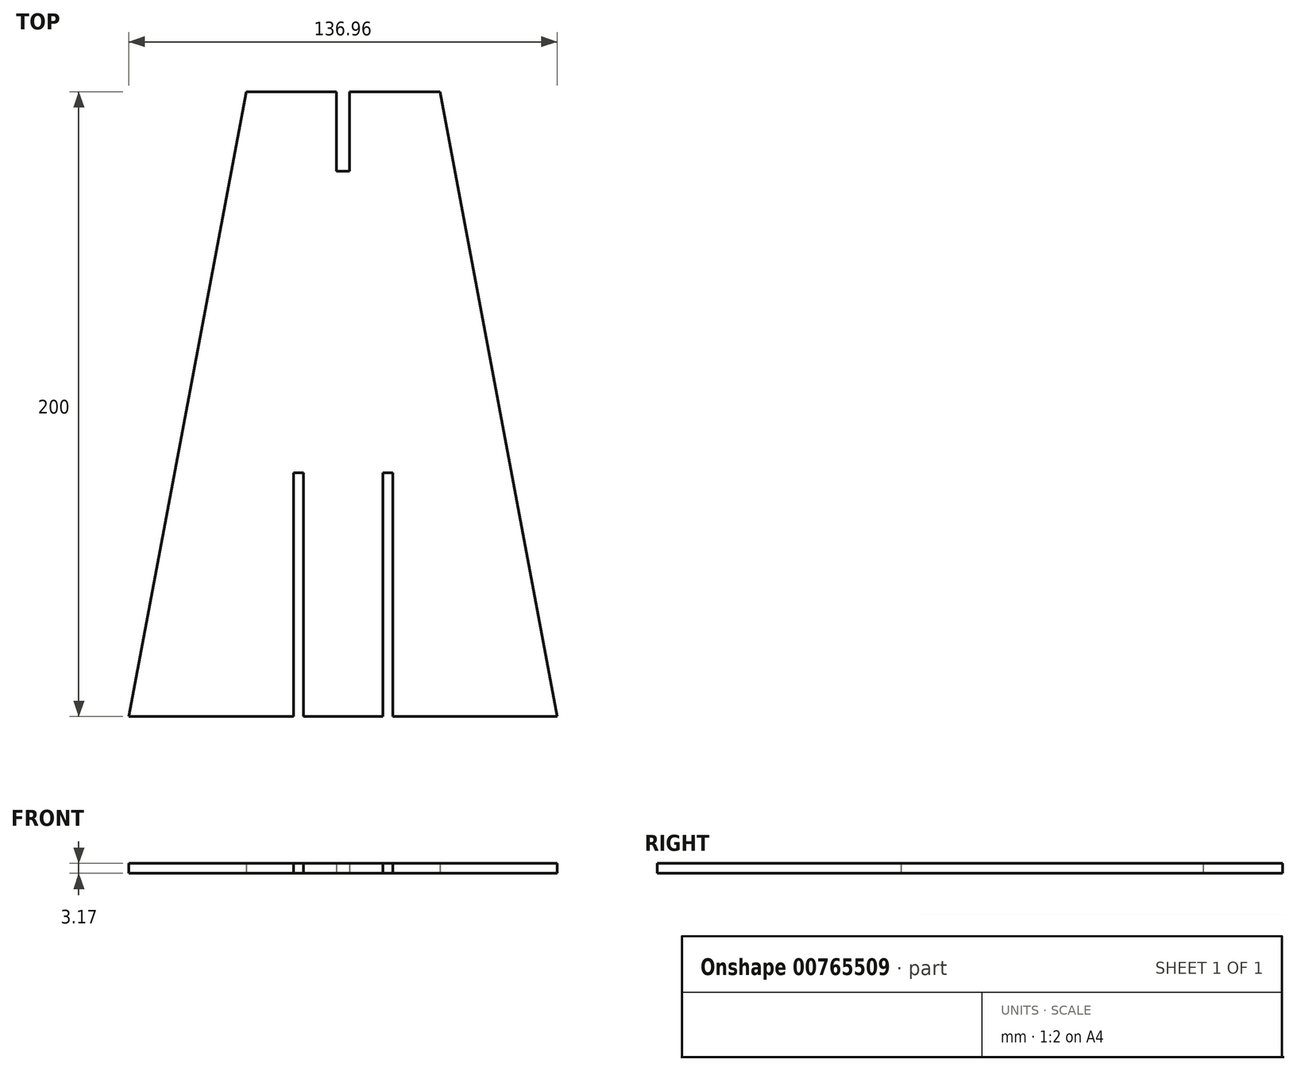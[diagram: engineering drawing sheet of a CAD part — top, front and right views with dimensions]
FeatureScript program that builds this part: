
annotation { "Feature Type Name" : "Feature", "Feature Type Description" : "" }
export const myFeature = defineFeature(function(context is Context, id is Id, definition is map)
    precondition{}
    {
        {
            var Q0;
            Q0=qCreatedBy(makeId("Top.planeOp"),FACE);
            var sketch = newSketch(context, id + "F0", { "sketchPlane" : qUnion([Q0])});
            skLineSegment(sketch, "E0", {"start": v(0, 0) * mm, "end": v(73.41, 0) * mm});
            skLineSegment(sketch, "E1", {"start": v(37.5, 200) * mm, "end": v(66.37, 200) * mm});
            skPoint(sketch, "E2", {"position": v(68.48, 200) * mm});
            skPoint(sketch, "E3", {"position": v(68.48, 0) * mm});
            skLineSegment(sketch, "E4", {"start": v(99.46, 200) * mm, "end": v(136.96, 0) * mm});
            skLineSegment(sketch, "E5", {"start": v(37.5, 200) * mm, "end": v(0, 0) * mm});
            skPoint(sketch, "E6", {"position": v(73.41, 0) * mm});
            skPoint(sketch, "E7", {"position": v(76.59, 0) * mm});
            skLineSegment(sketch, "E8.bottom", {"start": v(76.59, 276) * mm, "end": v(73.41, 276) * mm});
            skLineSegment(sketch, "E9.trimOffspring", {"start": v(76.59, 0) * mm, "end": v(136.96, 0) * mm});
            skLineSegment(sketch, "E10.trimOffspring", {"start": v(76.59, 200) * mm, "end": v(99.46, 200) * mm});
            skLineSegment(sketch, "E11", {"start": v(73.41, 0) * mm, "end": v(76.59, 0) * mm});
            skPoint(sketch, "E12", {"position": v(55.78, 0) * mm});
            skPoint(sketch, "E13", {"position": v(81.18, 0) * mm});
            skLineSegment(sketch, "E14.bottom", {"start": v(55.78, 0) * mm, "end": v(52.6, 0) * mm});
            skLineSegment(sketch, "E14.top", {"start": v(55.78, 78) * mm, "end": v(52.6, 78) * mm});
            skLineSegment(sketch, "E14.left", {"start": v(55.78, 0) * mm, "end": v(55.78, 78) * mm});
            skLineSegment(sketch, "E14.right", {"start": v(52.6, 0) * mm, "end": v(52.6, 78) * mm});
            skLineSegment(sketch, "E15.bottom", {"start": v(81.18, 0) * mm, "end": v(84.36, 0) * mm});
            skLineSegment(sketch, "E15.top", {"start": v(81.18, 78) * mm, "end": v(84.36, 78) * mm});
            skLineSegment(sketch, "E15.left", {"start": v(81.18, 0) * mm, "end": v(81.18, 78) * mm});
            skLineSegment(sketch, "E15.right", {"start": v(84.36, 0) * mm, "end": v(84.36, 78) * mm});
            skLineSegment(sketch, "E16", {"start": v(72.53, 200) * mm, "end": v(76.59, 200) * mm});
            skLineSegment(sketch, "E17", {"start": v(70.6, 200) * mm, "end": v(72.53, 200) * mm});
            skLineSegment(sketch, "E18.top", {"start": v(70.6, 174.6) * mm, "end": v(66.37, 174.6) * mm});
            skLineSegment(sketch, "E18.left", {"start": v(70.6, 200) * mm, "end": v(70.6, 174.6) * mm});
            skLineSegment(sketch, "E18.right", {"start": v(66.37, 200) * mm, "end": v(66.37, 174.6) * mm});
            skPoint(sketch, "E18.bottom.end.orphan", {"position": v(66.37, 225.4) * mm});
            skPoint(sketch, "E18.bottom.start.orphan", {"position": v(70.6, 225.4) * mm});
            skSolve(sketch);
        }
        {
            var Q0;
            Q0=makeQuery(id+"F0.imprint","IMPRINT",FACE,{"disambiguationData":[TD([[makeQuery(id+"F0.imprint","IMPRINT",EDGE,{"derivedFrom":sQuery(id+"F0.wireOp",EDGE,"E0")}),1.0]])]});
            extrude(context, id + "F1", {"entities" : qUnion([Q0]), "depth" : 3.17 * mm, "offsetDistance" : 25.4 * mm});
        }
    });
